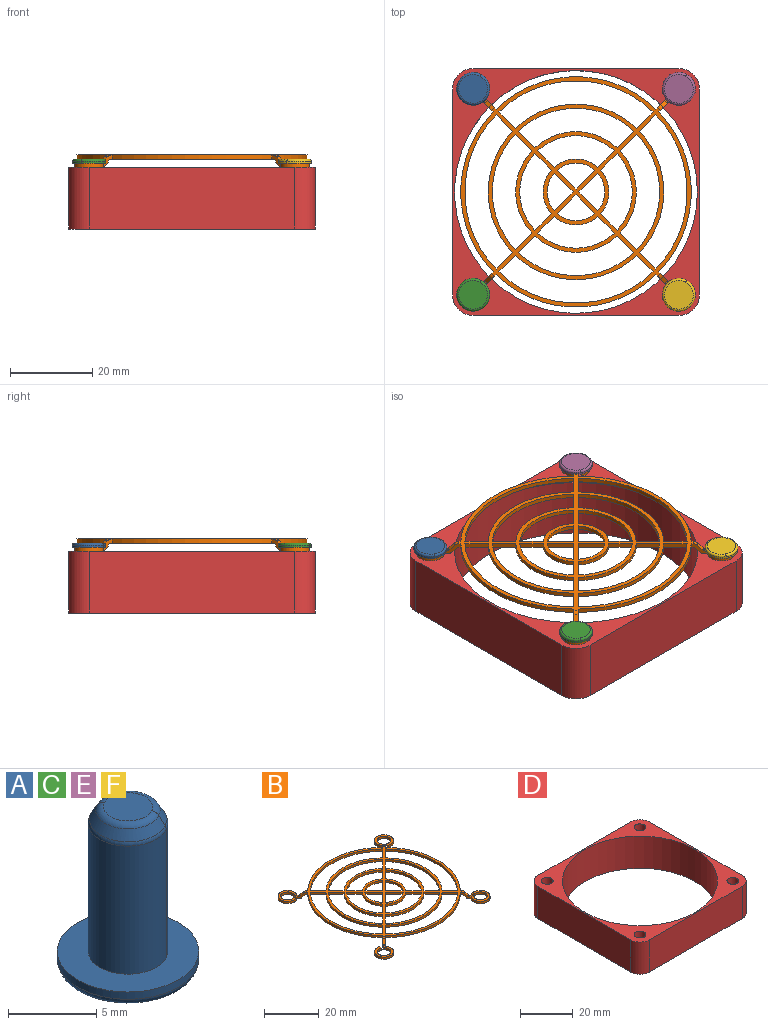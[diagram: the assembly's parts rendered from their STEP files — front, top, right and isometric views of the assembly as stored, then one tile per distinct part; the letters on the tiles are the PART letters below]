
ASSEMBLY  parts=6 mates=5
PART A: 15 faces, bbox 8.5x8.5x11 mm
  f0: plane 2.8x2.8mm, normal (0,0,1), area 6mm2, adj f1,f2
  f1: torus R=1.38mm, axis (0,0,1), area 2.7mm2, adj f0,f2,f4
  f2: torus R=1.38mm, axis (0,0,1), area 2.7mm2, adj f0,f1,f5
  f3: plane 7.09x7.09mm, normal (0,0,-1), area 38.5mm2, adj f6,f7
  f4: revolved ~4.1x3.23mm, area 4.6mm2, adj f1,f5,f8
  f5: revolved ~4.1x3.23mm, area 4.6mm2, adj f2,f4,f9
  f6: torus R=3.5mm, axis (0,0,1), area 9.4mm2, adj f3,f7,f10
  f7: torus R=3.5mm, axis (0,0,1), area 9.4mm2, adj f3,f6,f11
  f8: torus R=1.75mm, axis (0,0,1), area 1.8mm2, adj f4,f9,f12
  f9: torus R=1.75mm, axis (0,0,1), area 1.8mm2, adj f5,f8,f13
  f10: cylinder r=4mm len=7.51mm, axis (0,0,1), area 6.3mm2, adj f6,f11,f14
  f11: cylinder r=4mm len=7.51mm, axis (0,0,1), area 6.3mm2, adj f7,f10,f14
  f12: cylinder r=2.25mm len=8.87mm, axis (0,0,1), area 62.7mm2, adj f8,f13,f14
  f13: cylinder r=2.25mm len=8.87mm, axis (0,0,1), area 62.7mm2, adj f9,f12,f14
  f14: plane 8.14x8.14mm, normal (0,0,1), area 34.4mm2, adj f10,f11,f12,f13
PART B: 126 faces, bbox 57x57x3 mm
  f0: torus R=31.27mm, axis (0,0,-1), area 0.4mm2, adj f1,f13,f18,f21
  f1: cone r=30.92mm half-angle=45deg, axis (0,0,-1), area 2mm2, adj f0,f2,f18,f21
  f2: torus R=28.44mm, axis (0,0,-1), area 1.2mm2, adj f1,f12,f18,f21
  f3: torus R=31.27mm, axis (0,0,-1), area 0.4mm2, adj f4,f15,f22,f29
  f4: cone r=30.92mm half-angle=45deg, axis (0,0,-1), area 2mm2, adj f3,f5,f22,f29
  f5: torus R=28.44mm, axis (0,0,-1), area 1.2mm2, adj f4,f12,f22,f29
  f6: torus R=31.27mm, axis (0,0,-1), area 0.4mm2, adj f7,f14,f30,f33
  f7: cone r=30.92mm half-angle=45deg, axis (0,0,-1), area 2mm2, adj f6,f8,f30,f33
  f8: torus R=28.44mm, axis (0,0,-1), area 1.2mm2, adj f7,f12,f30,f33
  f9: torus R=31.27mm, axis (0,0,-1), area 0.4mm2, adj f10,f16,f17,f34
  f10: cone r=30.92mm half-angle=45deg, axis (0,0,-1), area 2mm2, adj f9,f11,f17,f34
  f11: torus R=28.44mm, axis (0,0,-1), area 1.2mm2, adj f10,f12,f17,f34
  f12: plane 56x56mm, normal (0,0,1), area 536.6mm2, adj f2,f5,f8,f11,f17,f18,f19,f21
  f13: plane 7x7mm, normal (0,0,1), area 18.4mm2, adj f0,f18,f20,f21,f24,f25,f26,f27
  f14: plane 7x7mm, normal (0,0,1), area 18.4mm2, adj f6,f30,f32,f33,f36,f37,f38,f39
  f15: plane 7x7mm, normal (0,0,1), area 18.4mm2, adj f3,f22,f28,f29,f40,f41,f42,f43
  f16: plane 7x7mm, normal (0,0,1), area 18.4mm2, adj f9,f17,f34,f44,f45,f46,f47,f48
  f17: plane 3.09x3.09mm, normal (0.71,-0.71,0), area 5.1mm2, adj f9,f10,f11,f12,f16,f19,f44,f112
  f18: plane 3.08x3.08mm, normal (0.71,0.71,0), area 5.1mm2, adj f0,f1,f2,f12,f13,f19,f27,f111
  f19: cylinder r=28mm len=38.88mm, axis (0,0,1), area 43mm2, adj f12,f17,f18,f124
  f20: plane 1x0.94mm, normal (-0.94,-0.34,0), area 1mm2, adj f13,f24,f26,f111
  f21: plane 3x2.76mm, normal (-0.71,-0.71,0), area 4.6mm2, adj f0,f1,f2,f12,f13,f23,f24,f111
  f22: plane 3x2.76mm, normal (0.71,-0.71,0), area 4.6mm2, adj f3,f4,f5,f12,f15,f23,f28,f109
  f23: cylinder r=28mm len=38.88mm, axis (0,0,1), area 43mm2, adj f12,f21,f22,f124
  f24: cylinder r=3.5mm len=7mm, axis (0,0,1), area 20mm2, adj f13,f20,f21,f111
  f25: plane 1x0.35mm, normal (0.71,0.71,0), area 0.5mm2, adj f13,f26,f27,f111
  f26: cylinder r=2.5mm len=5mm, axis (0,0,1), area 14.6mm2, adj f13,f20,f25,f111
  f27: plane 1x0.35mm, normal (0.71,-0.71,0), area 0.5mm2, adj f13,f18,f25,f111
  f28: cylinder r=3.5mm len=7mm, axis (0,0,1), area 20mm2, adj f15,f22,f43,f109
  f29: plane 3.08x3.08mm, normal (-0.71,0.71,0), area 5.1mm2, adj f3,f4,f5,f12,f15,f31,f40,f109
  f30: plane 3.09x3.09mm, normal (-0.71,-0.71,0), area 5.1mm2, adj f6,f7,f8,f12,f14,f31,f32,f110
  f31: cylinder r=28mm len=38.88mm, axis (0,0,1), area 43mm2, adj f12,f29,f30,f124
  f32: plane 1x0.35mm, normal (-0.71,0.71,0), area 0.5mm2, adj f14,f30,f39,f110
  f33: plane 3.01x2.76mm, normal (0.71,0.71,0), area 4.6mm2, adj f6,f7,f8,f12,f14,f35,f36,f110
  f34: plane 3.01x2.76mm, normal (-0.71,0.71,0), area 4.6mm2, adj f9,f10,f11,f12,f16,f35,f45,f112
  f35: cylinder r=28mm len=38.88mm, axis (0,0,1), area 43mm2, adj f12,f33,f34,f124
  f36: cylinder r=3.5mm len=7mm, axis (0,0,1), area 20mm2, adj f14,f33,f37,f110
  f37: plane 1x0.94mm, normal (0.94,0.34,0), area 1mm2, adj f14,f36,f38,f110
  f38: cylinder r=2.5mm len=5mm, axis (0,0,1), area 14.6mm2, adj f14,f37,f39,f110
  f39: plane 1x0.35mm, normal (-0.71,-0.71,0), area 0.5mm2, adj f14,f32,f38,f110
  f40: plane 1x0.35mm, normal (-0.71,-0.71,0), area 0.5mm2, adj f15,f29,f41,f109
  f41: plane 1x0.35mm, normal (-0.71,0.71,0), area 0.5mm2, adj f15,f40,f42,f109
  f42: cylinder r=2.5mm len=5mm, axis (0,0,1), area 14.6mm2, adj f15,f41,f43,f109
  f43: plane 1x0.94mm, normal (0.94,-0.34,0), area 1mm2, adj f15,f28,f42,f109
  f44: plane 1x0.35mm, normal (0.71,0.71,0), area 0.5mm2, adj f16,f17,f46,f125
  f45: cylinder r=3.5mm len=7mm, axis (0,0,1), area 20mm2, adj f16,f34,f48,f125
  f46: plane 1x0.35mm, normal (0.71,-0.71,0), area 0.5mm2, adj f16,f44,f47,f125
  f47: cylinder r=2.5mm len=5mm, axis (0,0,1), area 14.6mm2, adj f16,f46,f48,f125
  f48: plane 1x0.94mm, normal (-0.94,0.34,0), area 1mm2, adj f16,f45,f47,f125
  f49: plane 4.01x4.01mm, normal (0.71,-0.71,0), area 5.7mm2, adj f12,f51,f52,f124
  f50: plane 4.01x4.01mm, normal (0.71,0.71,0), area 5.7mm2, adj f12,f51,f52,f124
  f51: cylinder r=27mm len=37.47mm, axis (0,0,1), area 41.4mm2, adj f12,f49,f50,f124
  f52: cylinder r=21.33mm len=29.45mm, axis (0,0,1), area 32.5mm2, adj f12,f49,f50,f124
  f53: plane 4.01x4.01mm, normal (0.71,0.71,0), area 5.7mm2, adj f12,f55,f56,f124
  f54: plane 4.01x4.01mm, normal (-0.71,0.71,0), area 5.7mm2, adj f12,f55,f56,f124
  f55: cylinder r=27mm len=37.47mm, axis (0,0,1), area 41.4mm2, adj f12,f53,f54,f124
  f56: cylinder r=21.33mm len=29.45mm, axis (0,0,1), area 32.5mm2, adj f12,f53,f54,f124
  f57: plane 4.01x4.01mm, normal (-0.71,0.71,0), area 5.7mm2, adj f12,f59,f60,f124
  f58: plane 4.01x4.01mm, normal (-0.71,-0.71,0), area 5.7mm2, adj f12,f59,f60,f124
  f59: cylinder r=27mm len=37.47mm, axis (0,0,1), area 41.4mm2, adj f12,f57,f58,f124
  f60: cylinder r=21.33mm len=29.45mm, axis (0,0,1), area 32.5mm2, adj f12,f57,f58,f124
  f61: plane 4.01x4.01mm, normal (-0.71,-0.71,0), area 5.7mm2, adj f12,f63,f64,f124
  f62: plane 4.01x4.01mm, normal (0.71,-0.71,0), area 5.7mm2, adj f12,f63,f64,f124
  f63: cylinder r=27mm len=37.47mm, axis (0,0,1), area 41.4mm2, adj f12,f61,f62,f124
  f64: cylinder r=21.33mm len=29.45mm, axis (0,0,1), area 32.5mm2, adj f12,f61,f62,f124
  f65: plane 4.01x4.01mm, normal (0.71,-0.71,0), area 5.7mm2, adj f12,f67,f68,f124
  f66: plane 4.01x4.01mm, normal (0.71,0.71,0), area 5.7mm2, adj f12,f67,f68,f124
  f67: cylinder r=20.33mm len=28.04mm, axis (0,0,1), area 30.9mm2, adj f12,f65,f66,f124
  f68: cylinder r=14.67mm len=20.02mm, axis (0,0,1), area 22mm2, adj f12,f65,f66,f124
  f69: plane 4.01x4.01mm, normal (0.71,0.71,0), area 5.7mm2, adj f12,f71,f72,f124
  f70: plane 4.01x4.01mm, normal (-0.71,0.71,0), area 5.7mm2, adj f12,f71,f72,f124
  f71: cylinder r=20.33mm len=28.04mm, axis (0,0,1), area 30.9mm2, adj f12,f69,f70,f124
  f72: cylinder r=14.67mm len=20.02mm, axis (0,0,1), area 22mm2, adj f12,f69,f70,f124
  f73: plane 4.01x4.01mm, normal (-0.71,0.71,0), area 5.7mm2, adj f12,f75,f76,f124
  f74: plane 4.01x4.01mm, normal (-0.71,-0.71,0), area 5.7mm2, adj f12,f75,f76,f124
  f75: cylinder r=20.33mm len=28.04mm, axis (0,0,1), area 30.9mm2, adj f12,f73,f74,f124
  f76: cylinder r=14.67mm len=20.02mm, axis (0,0,1), area 22mm2, adj f12,f73,f74,f124
  f77: plane 4.01x4.01mm, normal (-0.71,-0.71,0), area 5.7mm2, adj f12,f79,f80,f124
  f78: plane 4.01x4.01mm, normal (0.71,-0.71,0), area 5.7mm2, adj f12,f79,f80,f124
  f79: cylinder r=20.33mm len=28.04mm, axis (0,0,1), area 30.9mm2, adj f12,f77,f78,f124
  f80: cylinder r=14.67mm len=20.02mm, axis (0,0,1), area 22mm2, adj f12,f77,f78,f124
  f81: plane 4.01x4.01mm, normal (0.71,-0.71,0), area 5.7mm2, adj f12,f83,f84,f124
  f82: plane 4.01x4.01mm, normal (0.71,0.71,0), area 5.7mm2, adj f12,f83,f84,f124
  f83: cylinder r=8mm len=10.58mm, axis (0,0,1), area 11.6mm2, adj f12,f81,f82,f124
  f84: cylinder r=13.67mm len=18.61mm, axis (0,0,1), area 20.5mm2, adj f12,f81,f82,f124
  f85: plane 4.01x4.01mm, normal (0.71,0.71,0), area 5.7mm2, adj f12,f87,f88,f124
  f86: plane 4.01x4.01mm, normal (-0.71,0.71,0), area 5.7mm2, adj f12,f87,f88,f124
  f87: cylinder r=8mm len=10.58mm, axis (0,0,1), area 11.6mm2, adj f12,f85,f86,f124
  f88: cylinder r=13.67mm len=18.61mm, axis (0,0,1), area 20.5mm2, adj f12,f85,f86,f124
  f89: plane 4.01x4.01mm, normal (-0.71,0.71,0), area 5.7mm2, adj f12,f91,f92,f124
  f90: plane 4.01x4.01mm, normal (-0.71,-0.71,0), area 5.7mm2, adj f12,f91,f92,f124
  f91: cylinder r=8mm len=10.58mm, axis (0,0,1), area 11.6mm2, adj f12,f89,f90,f124
  f92: cylinder r=13.67mm len=18.61mm, axis (0,0,1), area 20.5mm2, adj f12,f89,f90,f124
  f93: plane 4.01x4.01mm, normal (-0.71,-0.71,0), area 5.7mm2, adj f12,f95,f96,f124
  f94: plane 4.01x4.01mm, normal (0.71,-0.71,0), area 5.7mm2, adj f12,f95,f96,f124
  f95: cylinder r=8mm len=10.58mm, axis (0,0,1), area 11.6mm2, adj f12,f93,f94,f124
  f96: cylinder r=13.67mm len=18.61mm, axis (0,0,1), area 20.5mm2, adj f12,f93,f94,f124
  f97: cylinder r=7mm len=9.17mm, axis (0,0,1), area 10mm2, adj f12,f98,f99,f124
  f98: plane 4.58x4.58mm, normal (0.71,0.71,0), area 6.5mm2, adj f12,f97,f99,f124
  f99: plane 4.58x4.58mm, normal (0.71,-0.71,0), area 6.5mm2, adj f12,f97,f98,f124
  f100: plane 4.58x4.58mm, normal (0.71,0.71,0), area 6.5mm2, adj f12,f101,f102,f124
  f101: cylinder r=7mm len=9.17mm, axis (0,0,1), area 10mm2, adj f12,f100,f102,f124
  f102: plane 4.58x4.58mm, normal (-0.71,0.71,0), area 6.5mm2, adj f12,f100,f101,f124
  f103: plane 4.58x4.58mm, normal (-0.71,0.71,0), area 6.5mm2, adj f12,f104,f105,f124
  f104: cylinder r=7mm len=9.17mm, axis (0,0,1), area 10mm2, adj f12,f103,f105,f124
  f105: plane 4.58x4.58mm, normal (-0.71,-0.71,0), area 6.5mm2, adj f12,f103,f104,f124
  f106: plane 4.58x4.58mm, normal (0.71,-0.71,0), area 6.5mm2, adj f12,f107,f108,f124
  f107: cylinder r=7mm len=9.17mm, axis (0,0,1), area 10mm2, adj f12,f106,f108,f124
  f108: plane 4.58x4.58mm, normal (-0.71,-0.71,0), area 6.5mm2, adj f12,f106,f107,f124
  f109: plane 7x7mm, normal (0,0,-1), area 18.4mm2, adj f22,f28,f29,f40,f41,f42,f43,f113
  f110: plane 7x7mm, normal (0,0,-1), area 18.4mm2, adj f30,f32,f33,f36,f37,f38,f39,f114
  f111: plane 7x7mm, normal (0,0,-1), area 18.4mm2, adj f18,f20,f21,f24,f25,f26,f27,f115
  f112: torus R=31.27mm, axis (0,0,-1), area 1.2mm2, adj f17,f34,f116,f125
  f113: torus R=31.27mm, axis (0,0,-1), area 1.2mm2, adj f22,f29,f109,f117
  f114: torus R=31.27mm, axis (0,0,-1), area 1.2mm2, adj f30,f33,f110,f118
  f115: torus R=31.27mm, axis (0,0,-1), area 1.2mm2, adj f18,f21,f111,f119
  f116: cone r=30.21mm half-angle=45deg, axis (0,0,-1), area 2mm2, adj f17,f34,f112,f120
  f117: cone r=30.21mm half-angle=45deg, axis (0,0,-1), area 2mm2, adj f22,f29,f113,f121
  f118: cone r=30.21mm half-angle=45deg, axis (0,0,-1), area 2mm2, adj f30,f33,f114,f122
  f119: cone r=30.21mm half-angle=45deg, axis (0,0,-1), area 2mm2, adj f18,f21,f115,f123
  f120: torus R=28.44mm, axis (0,0,-1), area 0.4mm2, adj f17,f34,f116,f124
  f121: torus R=28.44mm, axis (0,0,-1), area 0.4mm2, adj f22,f29,f117,f124
  f122: torus R=28.44mm, axis (0,0,-1), area 0.4mm2, adj f30,f33,f118,f124
  f123: torus R=28.44mm, axis (0,0,-1), area 0.4mm2, adj f18,f21,f119,f124
  f124: plane 56x56mm, normal (0,0,-1), area 536.6mm2, adj f17,f18,f19,f21,f22,f23,f29,f30
  f125: plane 7x7mm, normal (0,0,-1), area 18.4mm2, adj f17,f34,f44,f45,f46,f47,f48,f112
PART C: same geometry as A
PART D: 15 faces, bbox 60x60x15 mm
  f0: plane 50x15mm, normal (1,0,0), area 750mm2, adj f9,f10,f11,f14
  f1: plane 50x15mm, normal (0,1,0), area 750mm2, adj f9,f10,f11,f12
  f2: plane 50x15mm, normal (-1,0,0), area 750mm2, adj f9,f10,f12,f13
  f3: cylinder r=29.5mm len=59mm, axis (0,0,-1), area 2780.3mm2, adj f9,f10
  f4: cylinder r=2.25mm len=15mm, axis (0,0,-1), area 212.1mm2, adj f9,f10
  f5: cylinder r=2.25mm len=15mm, axis (0,0,-1), area 212.1mm2, adj f9,f10
  f6: cylinder r=2.25mm len=15mm, axis (0,0,-1), area 212.1mm2, adj f9,f10
  f7: cylinder r=2.25mm len=15mm, axis (0,0,-1), area 212.1mm2, adj f9,f10
  f8: plane 50x15mm, normal (0,-1,0), area 750mm2, adj f9,f10,f13,f14
  f9: plane 60x60mm, normal (0,0,1), area 781mm2, adj f0,f1,f2,f3,f4,f5,f6,f7
  f10: plane 60x60mm, normal (0,0,-1), area 781mm2, adj f0,f1,f2,f3,f4,f5,f6,f7
  f11: cylinder r=5mm len=15mm, axis (0,0,-1), area 117.8mm2, adj f0,f1,f9,f10
  f12: cylinder r=5mm len=15mm, axis (0,0,1), area 117.8mm2, adj f1,f2,f9,f10
  f13: cylinder r=5mm len=15mm, axis (0,0,-1), area 117.8mm2, adj f2,f8,f9,f10
  f14: cylinder r=5mm len=15mm, axis (0,0,1), area 117.8mm2, adj f0,f8,f9,f10
PART E: same geometry as A
PART F: same geometry as A
PLACE A rot(axis=(1,0,0),180deg) t=(-25,40.06,17)mm
PLACE B at identity
PLACE C rot(axis=(1,0,0),180deg) t=(-25,-10,17)mm
PLACE D at identity fixed
PLACE E rot(axis=(1,0,0),180deg) t=(25,40.06,17)mm
PLACE F rot(axis=(1,0,0),180deg) t=(25,-10,17)mm
MATE fastened E.f2 <-> B.f16  axis (0,0,-1) through (25,25.06,16)mm
MATE fastened C.f2 <-> B.f28  axis (0,0,-1) through (-25,-25,16)mm
MATE fastened A.f2 <-> B.f14  axis (0,0,-1) through (-25,25.06,16)mm
MATE fastened B.f28 <-> D.f5  axis (0,0,-1) through (-25,-25,15)mm
MATE fastened F.f2 <-> B.f24  axis (0,0,-1) through (25,-25,16)mm
